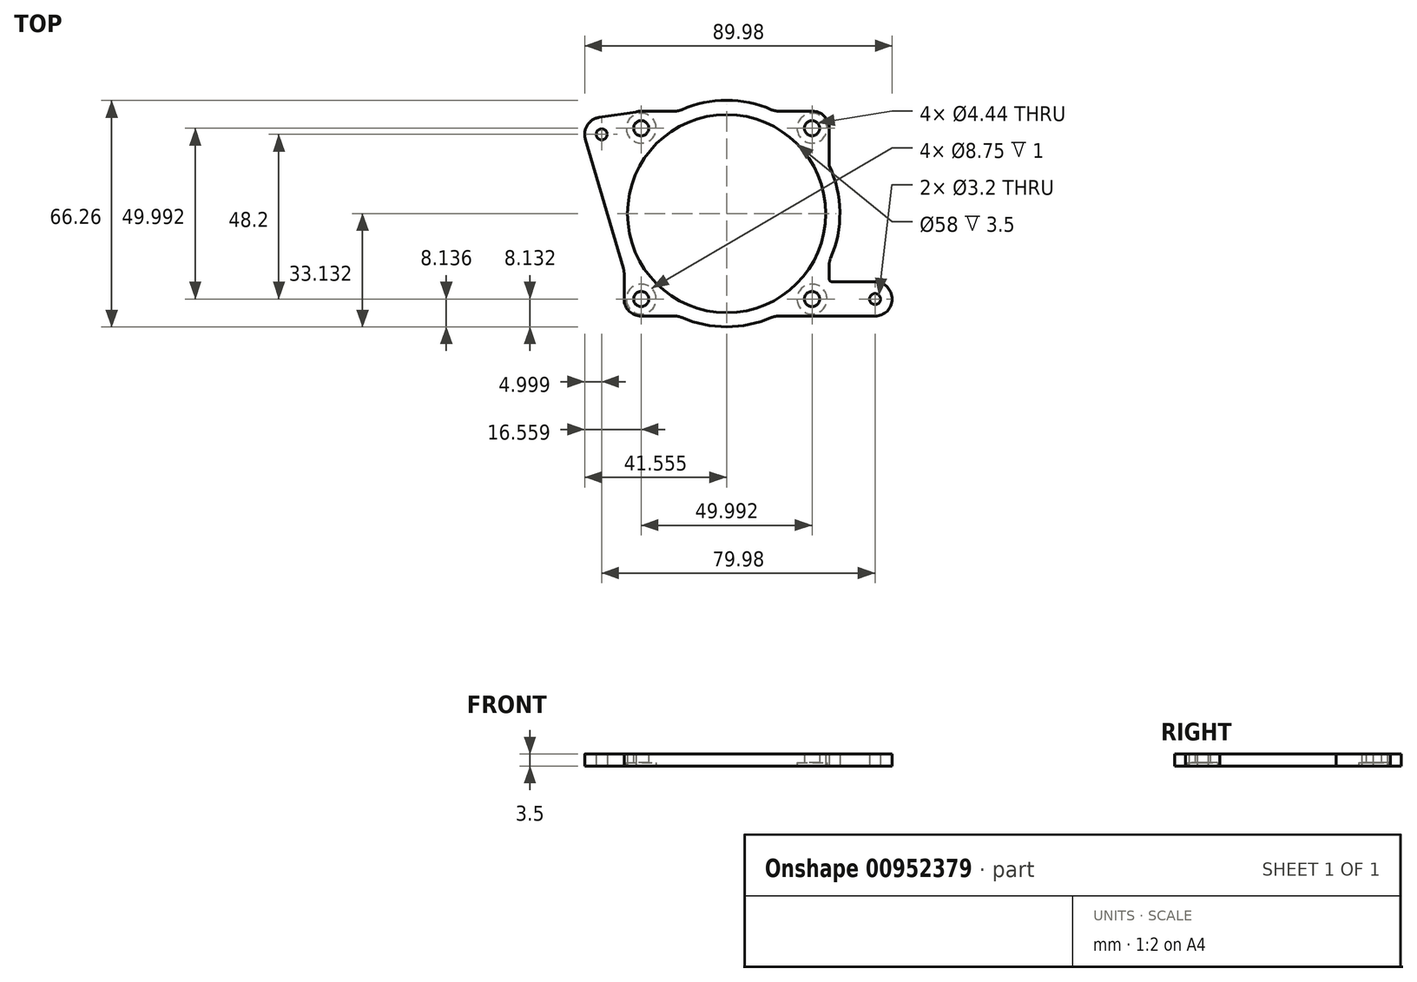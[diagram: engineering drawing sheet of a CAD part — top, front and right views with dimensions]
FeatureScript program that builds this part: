
annotation { "Feature Type Name" : "Feature", "Feature Type Description" : "" }
export const myFeature = defineFeature(function(context is Context, id is Id, definition is map)
    precondition{}
    {
        {
            var Q0;
            Q0=qCreatedBy(makeId("Top.planeOp"),FACE);
            var sketch = newSketch(context, id + "F0", { "sketchPlane" : qUnion([Q0])});
            skLineSegment(sketch, "E0.bottom", {"start": v(-53.42, 44.82) * mm, "end": v(48.18, 44.82) * mm, "construction": true});
            skLineSegment(sketch, "E0.top", {"start": v(-53.42, -8.48) * mm, "end": v(48.18, -8.48) * mm, "construction": true});
            skLineSegment(sketch, "E0.left", {"start": v(-53.42, 44.82) * mm, "end": v(-53.42, -8.48) * mm, "construction": true});
            skLineSegment(sketch, "E0.right", {"start": v(48.18, 44.82) * mm, "end": v(48.18, -8.48) * mm, "construction": true});
            skCircle(sketch, "E1", {"center": v(-39.42, -5.98) * mm, "radius": 1.6 * mm, "construction": true});
            skCircle(sketch, "E2", {"center": v(-38.12, 42.22) * mm, "radius": 1.6 * mm});
            skCircle(sketch, "E3", {"center": v(36.78, 42.22) * mm, "radius": 1.6 * mm, "construction": true});
            skCircle(sketch, "E4", {"center": v(41.86, -5.98) * mm, "radius": 1.6 * mm});
            skCircle(sketch, "E5", {"center": v(12.68, -0.88) * mm, "radius": 1.6 * mm, "construction": true});
            skCircle(sketch, "E6", {"center": v(12.68, 27.02) * mm, "radius": 1.6 * mm, "construction": true});
            skLineSegment(sketch, "E7.bottom", {"start": v(-26.56, 49.02) * mm, "end": v(-16.7, 49.02) * mm});
            skLineSegment(sketch, "E7.top", {"start": v(-26.56, -10.98) * mm, "end": v(-16.7, -10.98) * mm});
            skLineSegment(sketch, "E7.left", {"start": v(-31.56, 1.62) * mm, "end": v(-31.56, -5.98) * mm});
            skLineSegment(sketch, "E7.right", {"start": v(28.44, 44.02) * mm, "end": v(28.44, 33.08) * mm});
            skCircle(sketch, "E8", {"center": v(-26.56, 44.02) * mm, "radius": 2.22 * mm});
            skLineSegment(sketch, "E9", {"start": v(-31.56, 49.02) * mm, "end": v(28.44, -10.98) * mm, "construction": true});
            skLineSegment(sketch, "E10", {"start": v(28.44, 49.02) * mm, "end": v(-31.56, -10.98) * mm, "construction": true});
            skArc(sketch, "E11", {"start": v(-22.35, 44.82) * mm, "mid": v(-34.66, 17.59) * mm, "end": v(-20.04, -8.48) * mm, "construction": true});
            skCircle(sketch, "E12", {"center": v(23.43, 44.02) * mm, "radius": 2.22 * mm});
            skCircle(sketch, "E13", {"center": v(23.43, -5.97) * mm, "radius": 2.22 * mm});
            skCircle(sketch, "E14", {"center": v(-26.56, -5.97) * mm, "radius": 2.22 * mm});
            skPoint(sketch, "E15.visualSharp", {"position": v(28.44, 49.02) * mm});
            skArc(sketch, "E15.filletArc", {"start": v(28.44, 44.02) * mm, "mid": v(26.97, 47.56) * mm, "end": v(23.44, 49.02) * mm});
            skPoint(sketch, "E16.visualSharp", {"position": v(28.44, -10.98) * mm});
            skLineSegment(sketch, "E16.filletArc", {"start": v(23.44, -10.98) * mm, "end": v(23.44, -10.98) * mm});
            skPoint(sketch, "E17.visualSharp", {"position": v(-31.56, -10.98) * mm});
            skArc(sketch, "E17.filletArc", {"start": v(-31.56, -5.98) * mm, "mid": v(-30.1, -9.51) * mm, "end": v(-26.56, -10.98) * mm});
            skPoint(sketch, "E18.visualSharp", {"position": v(-31.56, 49.02) * mm});
            skArc(sketch, "E18.filletArc", {"start": v(-26.56, 49.02) * mm, "mid": v(-28.48, 48.64) * mm, "end": v(-30.1, 47.56) * mm});
            skPoint(sketch, "E19.19", {"position": v(-146.14, 42.5) * mm});
            skPoint(sketch, "E20.0", {"position": v(-66.16, -5.7) * mm});
            skPoint(sketch, "E21", {"position": v(-1.56, 17.8) * mm});
            skCircle(sketch, "E22", {"center": v(-1.56, 19.02) * mm, "radius": 29 * mm});
            skArc(sketch, "E23", {"start": v(-38.87, 47.17) * mm, "mid": v(-42.34, 44.9) * mm, "end": v(-42.92, 40.8) * mm});
            skLineSegment(sketch, "E24", {"start": v(-31.77, 3.04) * mm, "end": v(-42.92, 40.8) * mm});
            skLineSegment(sketch, "E25", {"start": v(-26.56, 49.02) * mm, "end": v(-38.87, 47.17) * mm});
            skLineSegment(sketch, "E26", {"start": v(41.86, -10.98) * mm, "end": v(23.44, -10.98) * mm});
            skPoint(sketch, "E27.visualSharp", {"position": v(46.86, 15.79) * mm});
            skLineSegment(sketch, "E28", {"start": v(37.65, 11.98) * mm, "end": v(37.65, 37.31) * mm, "construction": true});
            skLineSegment(sketch, "E29", {"start": v(37.65, 11.98) * mm, "end": v(37.65, -33.07) * mm, "construction": true});
            skArc(sketch, "E30.filletArc", {"start": v(-31.56, 1.62) * mm, "mid": v(-31.62, 2.33) * mm, "end": v(-31.77, 3.04) * mm});
            skArc(sketch, "E31.trimOffspring", {"start": v(37.53, -8.48) * mm, "mid": v(37.59, -8.58) * mm, "end": v(37.65, -8.67) * mm});
            skPoint(sketch, "E32.orphan", {"position": v(28.44, -5.98) * mm});
            skPoint(sketch, "E33.visualSharp", {"position": v(28.44, 35.44) * mm});
            skArc(sketch, "E34.trimOffspring", {"start": v(11.58, 49.43) * mm, "mid": v(-1.56, 52.15) * mm, "end": v(-14.71, 49.43) * mm});
            skArc(sketch, "E35.trimOffspring", {"start": v(-14.71, -11.39) * mm, "mid": v(-1.56, -14.1) * mm, "end": v(11.58, -11.39) * mm});
            skArc(sketch, "E36.trimOffspring", {"start": v(16.91, -8.48) * mm, "mid": v(21.2, -5.06) * mm, "end": v(24.85, -0.98) * mm, "construction": true});
            skLineSegment(sketch, "E37.trimOffspring", {"start": v(13.56, 49.02) * mm, "end": v(23.44, 49.02) * mm});
            skPoint(sketch, "E38.visualSharp", {"position": v(-15.62, 49.02) * mm});
            skArc(sketch, "E38.filletArc", {"start": v(-16.7, 49.02) * mm, "mid": v(-15.68, 49.13) * mm, "end": v(-14.71, 49.43) * mm});
            skPoint(sketch, "E39.visualSharp", {"position": v(12.5, 49.02) * mm});
            skArc(sketch, "E39.filletArc", {"start": v(11.58, 49.43) * mm, "mid": v(12.55, 49.13) * mm, "end": v(13.56, 49.02) * mm});
            skLineSegment(sketch, "E40.trimOffspring", {"start": v(13.56, -10.98) * mm, "end": v(23.44, -10.98) * mm});
            skPoint(sketch, "E41.visualSharp", {"position": v(-15.62, -10.98) * mm});
            skArc(sketch, "E41.filletArc", {"start": v(-14.71, -11.39) * mm, "mid": v(-15.68, -11.08) * mm, "end": v(-16.7, -10.98) * mm});
            skPoint(sketch, "E42.visualSharp", {"position": v(12.5, -10.98) * mm});
            skArc(sketch, "E42.filletArc", {"start": v(13.56, -10.98) * mm, "mid": v(12.55, -11.08) * mm, "end": v(11.58, -11.39) * mm});
            skCircle(sketch, "E43.converted", {"center": v(41.86, -5.98) * mm, "radius": 5 * mm});
            skLineSegment(sketch, "E44", {"start": v(41.86, -0.98) * mm, "end": v(29.44, -0.98) * mm});
            skLineSegment(sketch, "E45", {"start": v(24.85, -0.98) * mm, "end": v(24.85, -0.98) * mm});
            skLineSegment(sketch, "E46", {"start": v(28.44, 3.9) * mm, "end": v(28.44, 0.02) * mm});
            skArc(sketch, "E47.trimOffspring", {"start": v(28.85, 5.88) * mm, "mid": v(30.6, 26.97) * mm, "end": v(19.22, 44.82) * mm});
            skPoint(sketch, "E48.visualSharp", {"position": v(28.44, -0.98) * mm});
            skArc(sketch, "E48.filletArc", {"start": v(28.44, 0.02) * mm, "mid": v(28.73, -0.69) * mm, "end": v(29.44, -0.98) * mm});
            skPoint(sketch, "E49.visualSharp", {"position": v(28.44, 4.96) * mm});
            skArc(sketch, "E49.filletArc", {"start": v(28.85, 5.88) * mm, "mid": v(28.54, 4.9) * mm, "end": v(28.44, 3.9) * mm});
            skSolve(sketch);
        }
        {
            var Q0;
            Q0=qCreatedBy(makeId("Top.planeOp"),FACE);
            cPlane(context, id + "F1", {"entities" : qUnion([Q0]), "cplaneType" : CPlaneType.OFFSET, "offset" : 5 * mm, "oppositeDirection" : true, "width" : 150 * mm, "height" : 150 * mm});
        }
        {
            var Q0;
            Q0=qSketchRegion(id+"F0",true);
            extrude(context, id + "F2", {"entities" : qUnion([Q0]), "depth" : 3.5 * mm, "offsetDistance" : 25 * mm});
        }
        {
            var Q0;
            Q0=makeQuery(id+"F2.opExtrude","CAP_FACE",FACE,{"disambiguationData":[OSD([sQuery(id+"F0.wireOp",EDGE,"E2"),sQuery(id+"F0.wireOp",EDGE,"E4"),sQuery(id+"F0.wireOp",EDGE,"E7.bottom"),sQuery(id+"F0.wireOp",EDGE,"E7.top"),sQuery(id+"F0.wireOp",EDGE,"E7.left"),sQuery(id+"F0.wireOp",EDGE,"E7.right"),sQuery(id+"F0.wireOp",EDGE,"E8"),sQuery(id+"F0.wireOp",EDGE,"E12"),sQuery(id+"F0.wireOp",EDGE,"E13"),sQuery(id+"F0.wireOp",EDGE,"E14"),sQuery(id+"F0.wireOp",EDGE,"E15.filletArc"),sQuery(id+"F0.wireOp",EDGE,"E17.filletArc"),sQuery(id+"F0.wireOp",EDGE,"E18.filletArc"),sQuery(id+"F0.wireOp",EDGE,"E22"),sQuery(id+"F0.wireOp",EDGE,"E23"),sQuery(id+"F0.wireOp",EDGE,"curC7CVh-JOHb-7Mg7-MYZK-eGtlUkxcjdBB"),sQuery(id+"F0.wireOp",EDGE,"E24"),sQuery(id+"F0.wireOp",EDGE,"E25"),sQuery(id+"F0.wireOp",EDGE,"E26"),sQuery(id+"F0.wireOp",EDGE,"FxnBB36o-Rqyz-MdkS-9HdU-SdkZIjoqN9XQ"),sQuery(id+"F0.wireOp",EDGE,"PDu09gB8-Ofy4-FQeL-J0Lt-99pAvs8q4Kbb"),sQuery(id+"F0.wireOp",EDGE,"E27.filletArc"),sQuery(id+"F0.wireOp",EDGE,"gc8W9cHn-Bc5P-Qay7-8Ruc-CuvNxYl3HCNp"),sQuery(id+"F0.wireOp",EDGE,"KVewsBho-RE48-E0Hx-cDzr-HIZNmGF8zBQT"),sQuery(id+"F0.wireOp",EDGE,"5kwrPDOV-29eI-Kryb-Ag34-BUCpRlZNhAOB"),sQuery(id+"F0.wireOp",EDGE,"dNwue7Wm-2wzY-Y4re-vDyQ-YOXkvpwNrZ5r"),sQuery(id+"F0.wireOp",EDGE,"E30.filletArc"),sQuery(id+"F0.wireOp",EDGE,"E33.filletArc")])],"isStart":true});
            var sketch = newSketch(context, id + "F3", { "sketchPlane" : qUnion([Q0])});
            skCircle(sketch, "E50.0", {"center": v(-26.56, 5.97) * mm, "radius": 2.22 * mm});
            skCircle(sketch, "E50.1", {"center": v(23.43, 5.97) * mm, "radius": 2.22 * mm});
            skCircle(sketch, "E50.2", {"center": v(23.43, -44.02) * mm, "radius": 2.22 * mm});
            skCircle(sketch, "E50.3", {"center": v(-26.56, -44.02) * mm, "radius": 2.22 * mm});
            skCircle(sketch, "E51", {"center": v(23.43, 5.97) * mm, "radius": 4.38 * mm});
            skCircle(sketch, "E52", {"center": v(-26.56, 5.97) * mm, "radius": 4.38 * mm});
            skCircle(sketch, "E53", {"center": v(-26.56, -44.02) * mm, "radius": 4.38 * mm});
            skCircle(sketch, "E54", {"center": v(23.43, -44.02) * mm, "radius": 4.38 * mm});
            skSolve(sketch);
        }
        {
            var Q0;
            Q0=makeQuery(id+"F3.imprint","IMPRINT",FACE,{"disambiguationData":[TD([[makeQuery(id+"F3.imprint","IMPRINT",EDGE,{"derivedFrom":sQuery(id+"F3.wireOp",EDGE,"E50.2")}),1.0]])]});
            var Q1;
            Q1=makeQuery(id+"F3.imprint","IMPRINT",FACE,{"disambiguationData":[TD([[makeQuery(id+"F3.imprint","IMPRINT",EDGE,{"derivedFrom":sQuery(id+"F3.wireOp",EDGE,"E50.3")}),1.0]])]});
            var Q2;
            Q2=makeQuery(id+"F3.imprint","IMPRINT",FACE,{"disambiguationData":[TD([[makeQuery(id+"F3.imprint","IMPRINT",EDGE,{"derivedFrom":sQuery(id+"F3.wireOp",EDGE,"E50.1")}),1.0]])]});
            var Q3;
            Q3=makeQuery(id+"F3.imprint","IMPRINT",FACE,{"disambiguationData":[TD([[makeQuery(id+"F3.imprint","IMPRINT",EDGE,{"derivedFrom":sQuery(id+"F3.wireOp",EDGE,"E50.0")}),1.0]])]});
            extrude(context, id + "F4", {"entities" : qUnion([Q0, Q1, Q2, Q3]), "operationType" : NewBodyOperationType.REMOVE, "oppositeDirection" : true, "depth" : 1 * mm, "offsetDistance" : 25 * mm});
        }
    });
